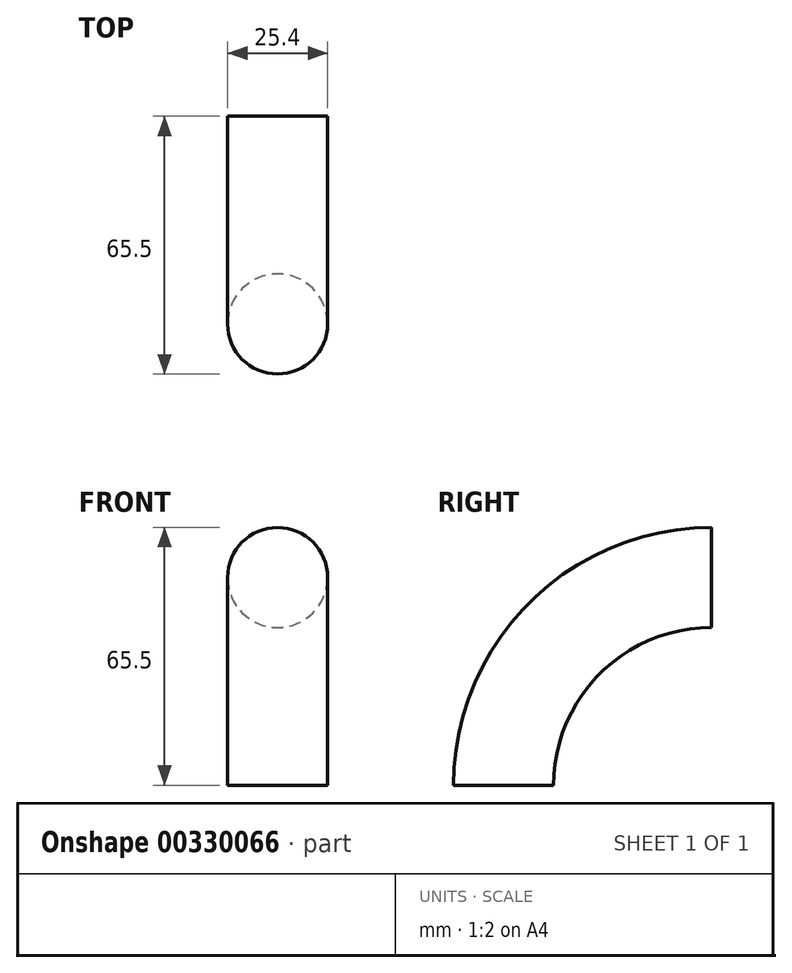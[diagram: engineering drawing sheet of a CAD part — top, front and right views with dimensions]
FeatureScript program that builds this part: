
annotation { "Feature Type Name" : "Feature", "Feature Type Description" : "" }
export const myFeature = defineFeature(function(context is Context, id is Id, definition is map)
    precondition{}
    {
        {
            var Q0;
            Q0=qCreatedBy(makeId("Top.planeOp"),FACE);
            var sketch = newSketch(context, id + "F0", { "sketchPlane" : qUnion([Q0])});
            skCircle(sketch, "E0", {"center": v(0, 0) * mm, "radius": 12.7 * mm});
            skSolve(sketch);
        }
        {
            var Q0;
            Q0=qCreatedBy(makeId("Top.planeOp"),FACE);
            var sketch = newSketch(context, id + "F1", { "sketchPlane" : qUnion([Q0])});
            skLineSegment(sketch, "E1", {"start": v(-13.6, 52.8) * mm, "end": v(17.46, 52.8) * mm});
            skSolve(sketch);
        }
        {
            var Q0;
            Q0=makeQuery(id+"F0.imprint","IMPRINT",FACE,{"disambiguationData":[TD([[makeQuery(id+"F0.imprint","IMPRINT",EDGE,{"derivedFrom":sQuery(id+"F0.wireOp",EDGE,"E0")}),1.0]])]});
            var Q1;
            Q1=sQuery(id+"F1.wireOp",EDGE,"E1");
            revolve(context, id + "F2", {"entities" : qUnion([Q0]), "axis" : qUnion([Q1]), "revolveType" : RevolveType.ONE_DIRECTION, "oppositeDirection" : true, "angle" : 90 * degree});
        }
    });
